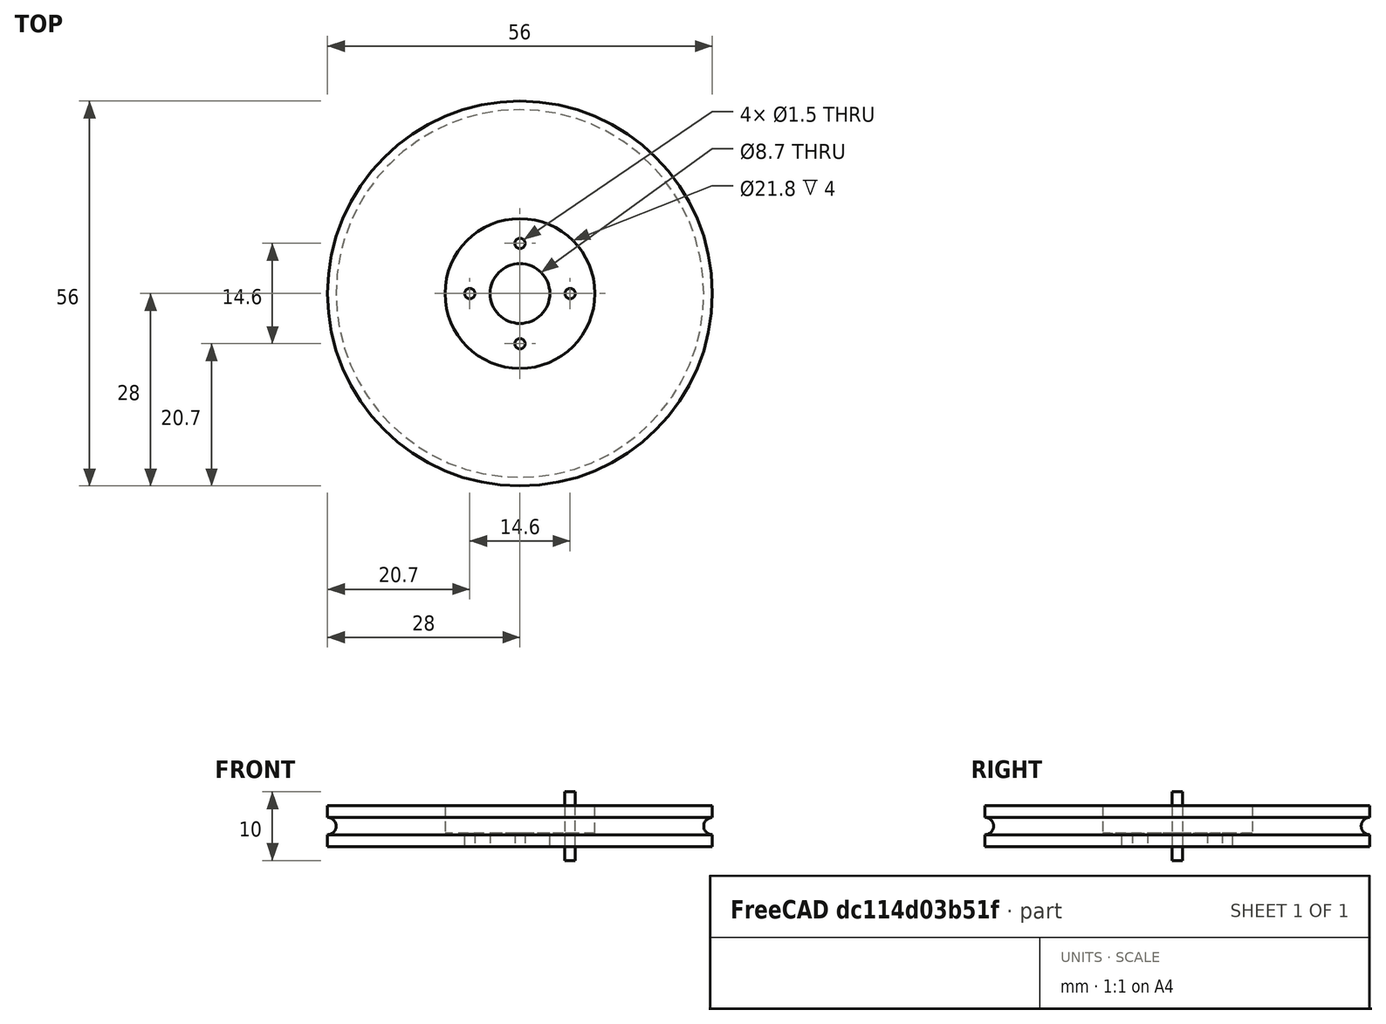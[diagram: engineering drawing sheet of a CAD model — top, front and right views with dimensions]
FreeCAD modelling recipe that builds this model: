
FCSTD DOCUMENT  (FreeCAD 0.21R33694 (Git))
Label: OJT1_T015P014_rueda_miniskybot
License: All rights reserved
LicenseURL: http://en.wikipedia.org/wiki/All_rights_reserved
objects: Part::Cylinder×4, Part::Cut×4, Part::Torus×1, Part::FeaturePython×1
note: 9 computed .brp shape members not serialized (recipe doc carries the construction recipe); baked Part::Feature solids carry a one-line shape summary decoded from their .brp

FEATURE [Part::Cylinder] Cylinder  label="rueda_base"
  Angle = 360
  AttacherType = Attacher::AttachEngine3D
  FirstAngle = 0
  Height = 6
  Placement = pos=(0,0,-3) rot=(0,0,1;0rad)
  Radius = 28
  SecondAngle = 0
FEATURE [Part::Torus] Torus  label="junta_torica"
  Angle1 = -180
  Angle2 = 180
  Angle3 = 360
  AttacherType = Attacher::AttachEngine3D
  Radius1 = 28
  Radius2 = 1.25
FEATURE [Part::Cut] Cut  label="rueda_basica"
  Base = -> Cylinder
  Refine = true
  Tool = -> Torus
FEATURE [Part::Cylinder] Cylinder001  label="Cylinder"
  Angle = 360
  AttacherType = Attacher::AttachEngine3D
  FirstAngle = 0
  Height = 10
  Placement = pos=(0,0,-1) rot=(0,0,1;0rad)
  Radius = 10.9
  SecondAngle = 0
FEATURE [Part::Cut] Cut001  label="rueda_con_hueco_corona"
  Base = -> Cut
  Refine = true
  Tool = -> Cylinder001
FEATURE [Part::Cylinder] Cylinder002  label="hueco_eje"
  Angle = 360
  AttacherType = Attacher::AttachEngine3D
  FirstAngle = 0
  Height = 10
  Placement = pos=(0,0,-10) rot=(0,0,1;0rad)
  Radius = 4.35
  SecondAngle = 0
FEATURE [Part::Cut] Cut002  label="rueda_corona_eje"
  Base = -> Cut001
  Refine = true
  Tool = -> Cylinder002
FEATURE [Part::Cylinder] Cylinder003  label="taladro"
  Angle = 360
  AttacherType = Attacher::AttachEngine3D
  FirstAngle = 0
  Height = 10
  Placement = pos=(7.3,0,-5) rot=(0,0,1;0rad)
  Radius = 0.75
  SecondAngle = 0
FEATURE [Part::FeaturePython] Array  # Draft array (typed FeaturePython)
  AlwaysSyncPlacement = false
  Angle = 360
  ArrayType = 1
  Axis = (0,0,1)
  Base = -> Cylinder003
  Center = (0,0,0)
  Count = 4
  ExpandArray = false
  Fuse = false
  IntervalAxis = (0,0,0)
  IntervalX = (100,0,0)
  IntervalY = (0,100,0)
  IntervalZ = (0,0,100)
  NumberCircles = 3
  NumberPolar = 4
  NumberX = 2
  NumberY = 2
  NumberZ = 1
  PlacementList = 4 placements: [(7.3,0,-5),(0,7.3,-5),(-7.3,8.93992e-16,-5),(-1.62093e-15,-7.3,-5)]
  RadialDistance = 50
  ScaleList = (4) [(1,1,1),(1,1,1),(1,1,1),(1,1,1)]
  Symmetry = 1
  TangentialDistance = 25
FEATURE [Part::Cut] Cut003
  Base = -> Cut002
  Refine = true
  Tool = -> Array
